# Revit family: 602-1-002-DN225-300
name_source: partatom
category: Pipe Accessories
units: mm (PartAtom-declared; Revit-internal decimal feet)

## family parameters
Always vertical = Yes
Cut with Voids When Loaded = No
Part Type = Valve - Breaks Into
Round Connector Dimension = Use Diameter
Shared = No
Work Plane-Based = No

## types (8) — shared parameters
B2 = 123 mm
Body_height = 245 mm
Body_height_ref = 233 mm
DN200 - 225_193-215 = 602-215-268-6100
DN200 - 225_218-242 = 602-242-268-6100
DN225 - 250_242-268 = 602-268-292-6100
DN250 - 250_266-292 = 602-292-306-6100
DN250 - 300_266-292 = 602-292-327-6100
DN300 - 300_301-327 = 602-327-350-6100
DN300 - 350_ 301-327 = 602-327-378-6100
DN300 - 350_324-350 = 602-350-378-6100
Description_ = AVK UNIVERSAL SUPA® STEP COUPLING
F = 5 mm  [stored 0.0164042 ft]
Search_Table = 602-1-002-DN225-300
URL_product_pages = https://www.avkvalves.com
W1 = 32 mm  [stored 0.104987 ft]

## per-type parameters (varying)
| type | Cut | Cut3 | Cut_2 | D | D(Adddon) | D2 | D2(Addon) | D3 | D3(Addon) | D4(Addon) | DN | DN1 | DN2 | DN225 | DN250 | DN300 | ID | L | L1 | PCD | PCD(Addon) | PCD/2 | W2 | W2(Addon) |
| DN200 - 225_193-215 | 134 mm | 108 mm | 134 mm | 165 mm | 181 mm | 135 mm  [stored 0.442913 ft] | 154 mm  [stored 0.505249 ft] | 386 mm | 425 mm | 128 mm | 225 mm | 268 mm | 215 mm | Yes | No | No | 113 mm | 257 mm | 140 mm  [stored 0.459318 ft] | 350 mm | 193 mm | 175 mm  [stored 0.574147 ft] | 188 mm  [stored 0.616798 ft] | 207 mm |
| DN200 - 225_218-242 | 134 mm | 121 mm  [stored 0.396982 ft] | 134 mm | 165 mm | 181 mm | 135 mm  [stored 0.442913 ft] | 154 mm  [stored 0.505249 ft] | 386 mm | 425 mm | 141 mm | 225 mm | 268 mm | 242 mm | Yes | No | No | 113 mm | 257 mm | 140 mm  [stored 0.459318 ft] | 350 mm | 193 mm | 175 mm  [stored 0.574147 ft] | 188 mm  [stored 0.616798 ft] | 207 mm |
| DN225 - 250_242-268 | 146 mm  [stored 0.479003 ft] | 134 mm | 146 mm  [stored 0.479003 ft] | 184 mm  [stored 0.603675 ft] | 202 mm | 147 mm  [stored 0.482283 ft] | 166 mm  [stored 0.544619 ft] | 425 mm | 468 mm | 154 mm  [stored 0.505249 ft] | 250 mm | 292 mm | 268 mm | No | Yes | No | 125 mm  [stored 0.410105 ft] | 277 mm | 160 mm  [stored 0.524934 ft] | 388 mm | 213 mm | 194 mm  [stored 0.636483 ft] | 208 mm | 228 mm |
| DN250 - 250_266-292 | 153 mm  [stored 0.501969 ft] | 146 mm  [stored 0.479003 ft] | 153 mm  [stored 0.501969 ft] | 184 mm  [stored 0.603675 ft] | 202 mm | 154 mm  [stored 0.505249 ft] | 173 mm  [stored 0.567585 ft] | 425 mm | 468 mm | 166 mm  [stored 0.544619 ft] | 250 mm | 306 mm | 292 mm | No | Yes | No | 125 mm  [stored 0.410105 ft] | 277 mm | 160 mm  [stored 0.524934 ft] | 388 mm | 213 mm | 194 mm  [stored 0.636483 ft] | 208 mm | 228 mm |
| DN250 - 300_266-292 | 164 mm | 146 mm  [stored 0.479003 ft] | 164 mm | 205 mm  [stored 0.672572 ft] | 226 mm | 165 mm | 184 mm  [stored 0.603675 ft] | 469 mm | 516 mm | 166 mm  [stored 0.544619 ft] | 300 mm | 327 mm | 292 mm | No | No | Yes | 150 mm | 277 mm | 160 mm  [stored 0.524934 ft] | 428 mm | 235 mm | 214 mm  [stored 0.7021 ft] | 230 mm | 252 mm |
| DN300 - 300_301-327 | 175 mm  [stored 0.574147 ft] | 164 mm | 175 mm  [stored 0.574147 ft] | 205 mm  [stored 0.672572 ft] | 226 mm | 176 mm  [stored 0.577428 ft] | 195 mm  [stored 0.639764 ft] | 469 mm | 516 mm | 184 mm  [stored 0.603675 ft] | 300 mm | 350 mm | 327 mm | No | No | Yes | 150 mm | 277 mm | 160 mm  [stored 0.524934 ft] | 428 mm | 235 mm | 214 mm  [stored 0.7021 ft] | 230 mm | 252 mm |
| DN300 - 350_324-350 | 189 mm  [stored 0.620079 ft] | 175 mm  [stored 0.574147 ft] | 189 mm  [stored 0.620079 ft] | 205 mm  [stored 0.672572 ft] | 226 mm | 190 mm | 209 mm  [stored 0.685696 ft] | 469 mm | 516 mm | 195 mm  [stored 0.639764 ft] | 300 mm | 378 mm | 350 mm | No | No | Yes | 150 mm | 277 mm | 160 mm  [stored 0.524934 ft] | 428 mm | 235 mm | 214 mm  [stored 0.7021 ft] | 230 mm | 252 mm |
| DN300 - 350_ 301-327 | 189 mm  [stored 0.620079 ft] | 164 mm | 189 mm  [stored 0.620079 ft] | 205 mm  [stored 0.672572 ft] | 226 mm | 190 mm | 209 mm  [stored 0.685696 ft] | 469 mm | 516 mm | 184 mm  [stored 0.603675 ft] | 300 mm | 378 mm | 327 mm | No | No | Yes | 150 mm | 277 mm | 160 mm  [stored 0.524934 ft] | 428 mm | 235 mm | 214 mm  [stored 0.7021 ft] | 230 mm | 252 mm |

note: [stored X ft] marks values corroborated as IEEE doubles in the binary element streams (Revit-internal decimal feet)

## geometry (parser evidence)
native form markers: Sweep x17
no freeform markers — native parametric forms only
